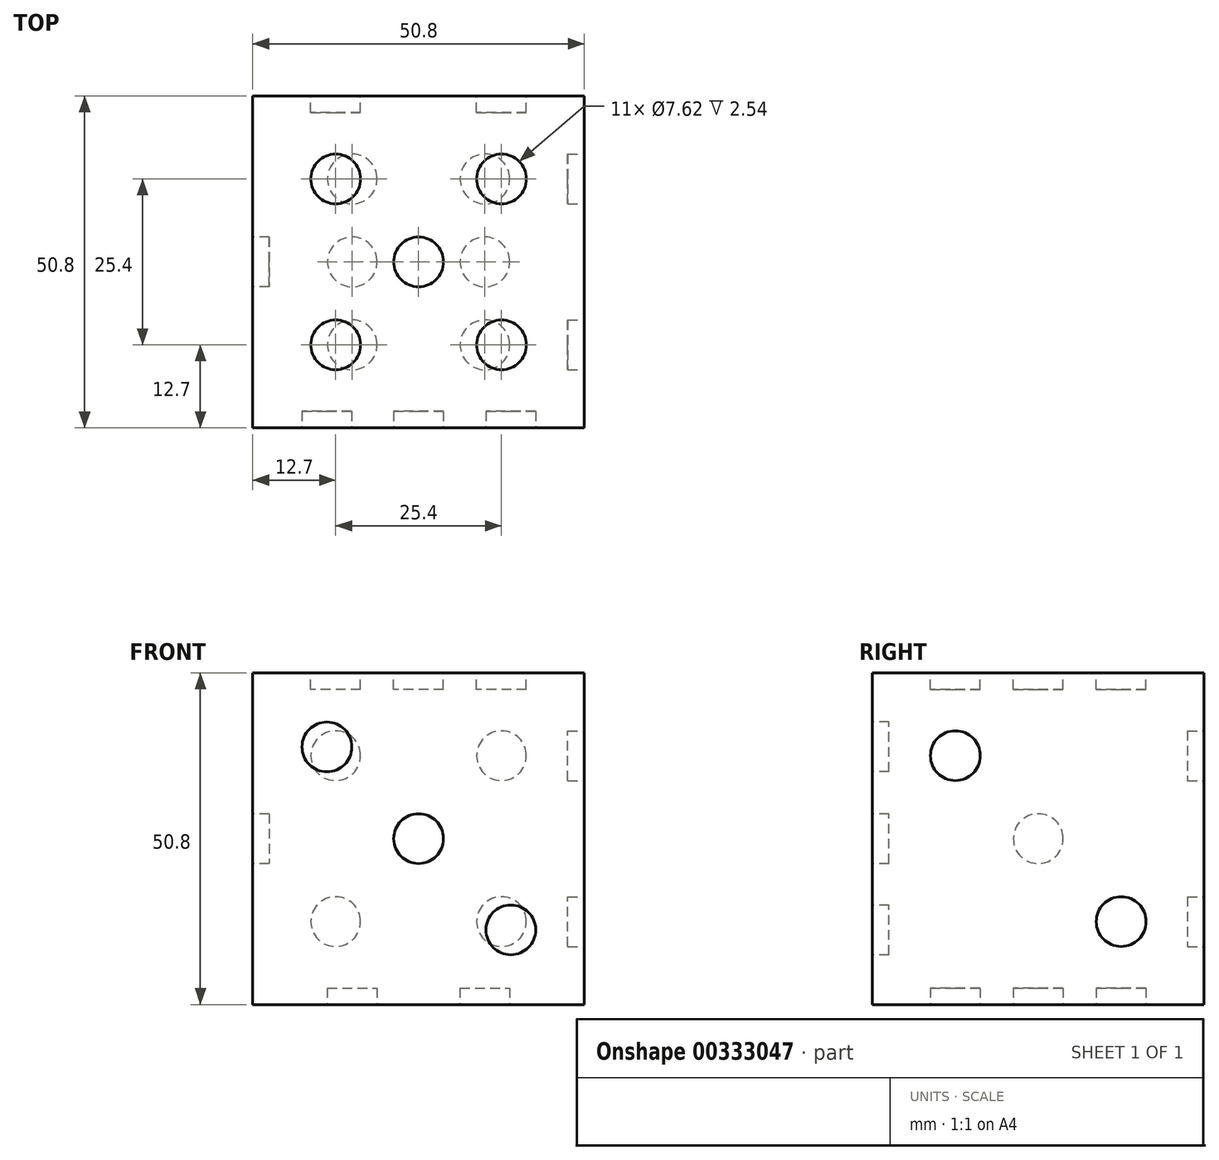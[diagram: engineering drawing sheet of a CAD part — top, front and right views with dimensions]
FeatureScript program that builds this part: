
annotation { "Feature Type Name" : "Feature", "Feature Type Description" : "" }
export const myFeature = defineFeature(function(context is Context, id is Id, definition is map)
    precondition{}
    {
        {
            var Q0;
            Q0=qCreatedBy(makeId("Front.planeOp"),FACE);
            var sketch = newSketch(context, id + "F0", { "sketchPlane" : qUnion([Q0])});
            skLineSegment(sketch, "E0.bottom", {"start": v(-76.2, -25.4) * mm, "end": v(-25.4, -25.4) * mm});
            skLineSegment(sketch, "E0.top", {"start": v(-76.2, -76.2) * mm, "end": v(-25.4, -76.2) * mm});
            skLineSegment(sketch, "E0.left", {"start": v(-76.2, -25.4) * mm, "end": v(-76.2, -76.2) * mm});
            skLineSegment(sketch, "E0.right", {"start": v(-25.4, -25.4) * mm, "end": v(-25.4, -76.2) * mm});
            skSolve(sketch);
        }
        {
            var Q0;
            Q0=makeQuery(id+"F0.imprint","IMPRINT",FACE,{"disambiguationData":[TD([[makeQuery(id+"F0.imprint","IMPRINT",EDGE,{"derivedFrom":sQuery(id+"F0.wireOp",EDGE,"E0.bottom")}),-1.0]])]});
            extrude(context, id + "F1", {"entities" : qUnion([Q0]), "depth" : 50.8 * mm});
        }
        {
            var Q0;
            Q0=makeQuery(id+"F1.opExtrude","SWEPT_FACE",FACE,{"disambiguationData":[OSD([sQuery(id+"F0.wireOp",EDGE,"E0.left")])]});
            var sketch = newSketch(context, id + "F2", { "sketchPlane" : qUnion([Q0])});
            skCircle(sketch, "E1", {"center": v(25.4, -50.8) * mm, "radius": 3.81 * mm});
            skSolve(sketch);
        }
        {
            var Q0;
            Q0 = qSketchRegion(id + "F2", true);
            extrude(context, id + "F3", {"entities" : qUnion([Q0]), "operationType" : NewBodyOperationType.REMOVE, "oppositeDirection" : true, "depth" : 2.54 * mm});
        }
        {
            var Q0;
            Q0=makeQuery(id+"F1.opExtrude","SWEPT_FACE",FACE,{"disambiguationData":[OSD([sQuery(id+"F0.wireOp",EDGE,"E0.right")])]});
            var sketch = newSketch(context, id + "F4", { "sketchPlane" : qUnion([Q0])});
            skCircle(sketch, "E2", {"center": v(-12.7, -63.5) * mm, "radius": 3.81 * mm});
            skCircle(sketch, "E3", {"center": v(-38.1, -38.1) * mm, "radius": 3.81 * mm});
            skSolve(sketch);
        }
        {
            var Q0;
            Q0 = qSketchRegion(id + "F4", true);
            extrude(context, id + "F5", {"entities" : qUnion([Q0]), "operationType" : NewBodyOperationType.REMOVE, "oppositeDirection" : true, "depth" : 2.54 * mm});
        }
        {
            var Q0;
            Q0=makeQuery(id+"F1.opExtrude","CAP_FACE",FACE,{"disambiguationData":[OSD([sQuery(id+"F0.wireOp",EDGE,"E0.bottom"),sQuery(id+"F0.wireOp",EDGE,"E0.top"),sQuery(id+"F0.wireOp",EDGE,"E0.left"),sQuery(id+"F0.wireOp",EDGE,"E0.right")])],"isStart":false});
            var sketch = newSketch(context, id + "F6", { "sketchPlane" : qUnion([Q0])});
            skCircle(sketch, "E4", {"center": v(-50.8, -50.8) * mm, "radius": 3.81 * mm});
            skPoint(sketch, "E4.centerSnap0", {"position": v(-50.8, -25.4) * mm});
            skCircle(sketch, "E5", {"center": v(-64.85, -36.75) * mm, "radius": 3.81 * mm});
            skCircle(sketch, "E6", {"center": v(-36.68, -64.77) * mm, "radius": 3.81 * mm});
            skSolve(sketch);
        }
        {
            var Q0;
            Q0 = qSketchRegion(id + "F6", true);
            extrude(context, id + "F7", {"entities" : qUnion([Q0]), "operationType" : NewBodyOperationType.REMOVE, "oppositeDirection" : true, "depth" : 2.54 * mm});
        }
        {
            var Q0;
            Q0=makeQuery(id+"F1.opExtrude","CAP_FACE",FACE,{"disambiguationData":[OSD([sQuery(id+"F0.wireOp",EDGE,"E0.bottom"),sQuery(id+"F0.wireOp",EDGE,"E0.top"),sQuery(id+"F0.wireOp",EDGE,"E0.left"),sQuery(id+"F0.wireOp",EDGE,"E0.right")])],"isStart":true});
            var sketch = newSketch(context, id + "F8", { "sketchPlane" : qUnion([Q0])});
            skCircle(sketch, "E7", {"center": v(38.1, -38.1) * mm, "radius": 3.81 * mm});
            skCircle(sketch, "E8", {"center": v(63.5, -38.1) * mm, "radius": 3.81 * mm});
            skCircle(sketch, "E9", {"center": v(38.1, -63.5) * mm, "radius": 3.81 * mm});
            skCircle(sketch, "E10", {"center": v(63.5, -63.5) * mm, "radius": 3.81 * mm});
            skSolve(sketch);
        }
        {
            var Q0;
            Q0 = qSketchRegion(id + "F8", true);
            extrude(context, id + "F9", {"entities" : qUnion([Q0]), "operationType" : NewBodyOperationType.REMOVE, "oppositeDirection" : true, "depth" : 2.54 * mm});
        }
        {
            var Q0;
            Q0=makeQuery(id+"F1.opExtrude","SWEPT_FACE",FACE,{"disambiguationData":[OSD([sQuery(id+"F0.wireOp",EDGE,"E0.bottom")])]});
            var sketch = newSketch(context, id + "F10", { "sketchPlane" : qUnion([Q0])});
            skCircle(sketch, "E11", {"center": v(-63.5, -12.7) * mm, "radius": 3.81 * mm});
            skCircle(sketch, "E12", {"center": v(-38.1, -12.7) * mm, "radius": 3.81 * mm});
            skCircle(sketch, "E13", {"center": v(-63.5, -38.1) * mm, "radius": 3.81 * mm});
            skCircle(sketch, "E14", {"center": v(-38.1, -38.1) * mm, "radius": 3.81 * mm});
            skCircle(sketch, "E15", {"center": v(-50.8, -25.4) * mm, "radius": 3.81 * mm});
            skSolve(sketch);
        }
        {
            var Q0;
            Q0 = qSketchRegion(id + "F10", true);
            extrude(context, id + "F11", {"entities" : qUnion([Q0]), "operationType" : NewBodyOperationType.REMOVE, "oppositeDirection" : true, "depth" : 2.54 * mm});
        }
        {
            var Q0;
            Q0=makeQuery(id+"F1.opExtrude","SWEPT_FACE",FACE,{"disambiguationData":[OSD([sQuery(id+"F0.wireOp",EDGE,"E0.top")])]});
            var sketch = newSketch(context, id + "F12", { "sketchPlane" : qUnion([Q0])});
            skCircle(sketch, "E16", {"center": v(-60.96, 25.4) * mm, "radius": 3.81 * mm});
            skCircle(sketch, "E17", {"center": v(-60.96, 38.1) * mm, "radius": 3.81 * mm});
            skCircle(sketch, "E18", {"center": v(-60.96, 12.7) * mm, "radius": 3.81 * mm});
            skCircle(sketch, "E19", {"center": v(-40.64, 12.7) * mm, "radius": 3.81 * mm});
            skCircle(sketch, "E20", {"center": v(-40.64, 25.4) * mm, "radius": 3.81 * mm});
            skCircle(sketch, "E21", {"center": v(-40.64, 38.1) * mm, "radius": 3.81 * mm});
            skSolve(sketch);
        }
        {
            var Q0;
            Q0 = qSketchRegion(id + "F12", true);
            extrude(context, id + "F13", {"entities" : qUnion([Q0]), "operationType" : NewBodyOperationType.REMOVE, "oppositeDirection" : true, "depth" : 2.54 * mm});
        }
    });
